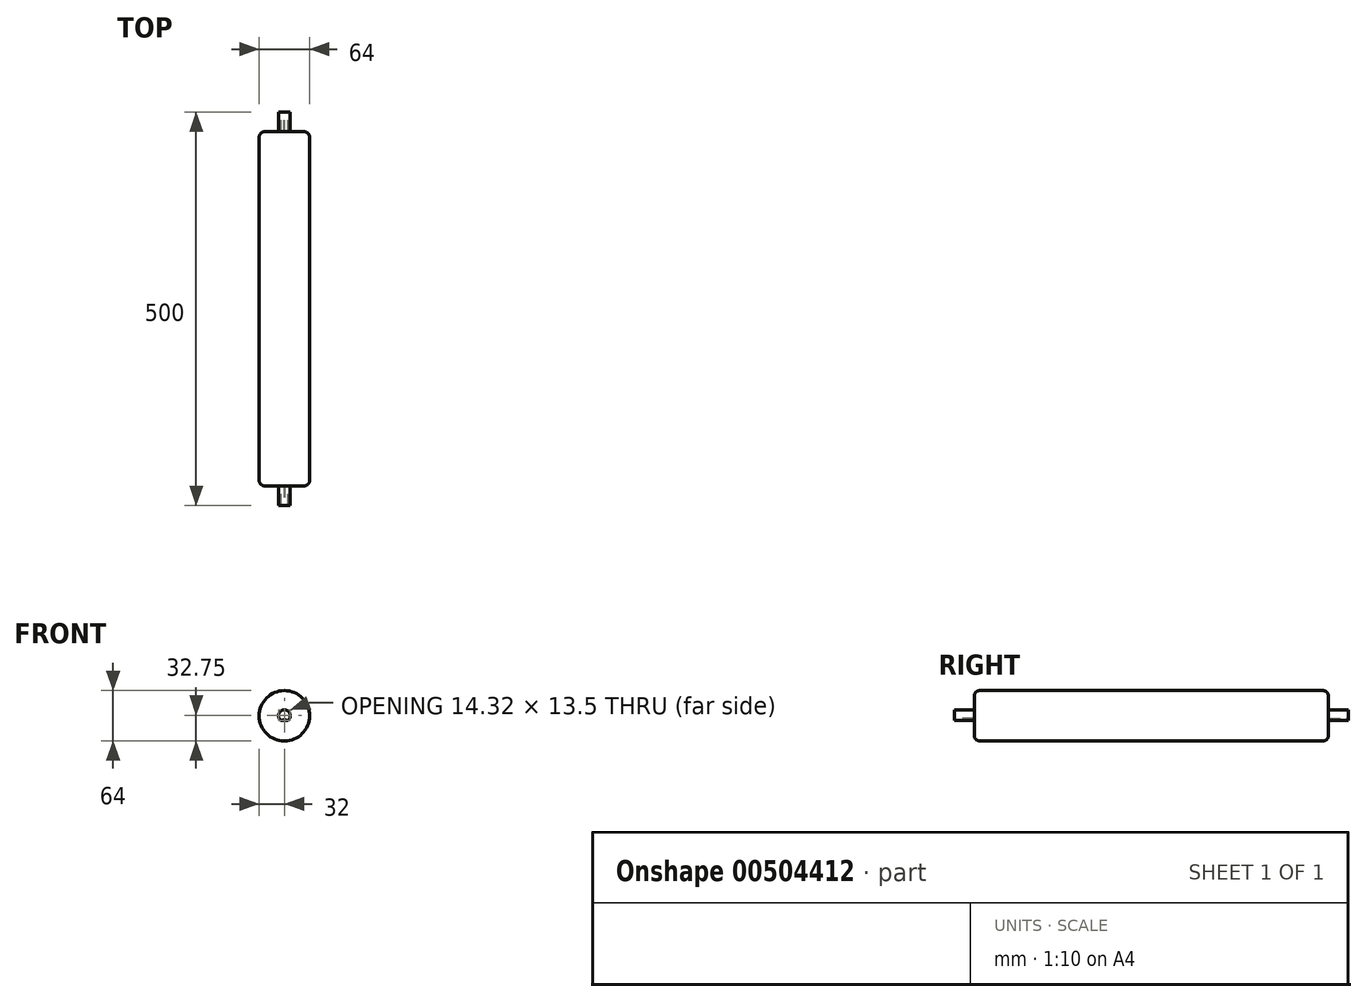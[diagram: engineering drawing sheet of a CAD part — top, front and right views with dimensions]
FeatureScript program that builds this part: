
annotation { "Feature Type Name" : "Feature", "Feature Type Description" : "" }
export const myFeature = defineFeature(function(context is Context, id is Id, definition is map)
    precondition{}
    {
        {
            var Q0;
            Q0=qCreatedBy(makeId("Right.planeOp"),FACE);
            var sketch = newSketch(context, id + "F0", { "sketchPlane" : qUnion([Q0])});
            skLineSegment(sketch, "E0", {"start": v(-237.76, 0) * mm, "end": v(-237.76, 7.5) * mm});
            skLineSegment(sketch, "E1", {"start": v(-237.76, 7.5) * mm, "end": v(-212.76, 7.5) * mm});
            skLineSegment(sketch, "E2", {"start": v(-212.76, 7.5) * mm, "end": v(-212.76, 32) * mm});
            skLineSegment(sketch, "E3", {"start": v(-212.76, 32) * mm, "end": v(237.24, 32) * mm});
            skLineSegment(sketch, "E4", {"start": v(237.24, 32) * mm, "end": v(237.24, 7.5) * mm});
            skLineSegment(sketch, "E5", {"start": v(237.24, 7.5) * mm, "end": v(262.24, 7.5) * mm});
            skLineSegment(sketch, "E6", {"start": v(262.24, 7.5) * mm, "end": v(262.24, 0) * mm});
            skLineSegment(sketch, "E7", {"start": v(262.24, 0) * mm, "end": v(-237.76, 0) * mm});
            skSolve(sketch);
        }
        {
            var Q0;
            Q0=makeQuery(id+"F0.imprint","IMPRINT",FACE,{"disambiguationData":[TD([[makeQuery(id+"F0.imprint","IMPRINT",EDGE,{"derivedFrom":sQuery(id+"F0.wireOp",EDGE,"E0")}),-1.0]])]});
            var Q1;
            Q1=sQuery(id+"F0.wireOp",EDGE,"E7");
            revolve(context, id + "F1", {"entities" : qUnion([Q0]), "axis" : qUnion([Q1]), "revolveType" : RevolveType.FULL});
        }
        {
            var Q0;
            Q0=makeQuery(id+"F1.opRevolve","SWEPT_EDGE",EDGE,{"disambiguationData":[OSD([sQuery(id+"F0.wireOp",EDGE,"E2"),sQuery(id+"F0.wireOp",EDGE,"E3")])]});
            var Q1;
            Q1=makeQuery(id+"F1.opRevolve","SWEPT_EDGE",EDGE,{"disambiguationData":[OSD([sQuery(id+"F0.wireOp",EDGE,"E3"),sQuery(id+"F0.wireOp",EDGE,"E4")])]});
            fillet(context, id + "F2", {"entities" : qUnion([Q0, Q1]), "radius" : 7 * mm, "tangentPropagation" : true, "allowEdgeOverflow" : false});
        }
        {
            var Q0;
            Q0=makeQuery(id+"F1.opRevolve","SWEPT_FACE",FACE,{"disambiguationData":[OSD([sQuery(id+"F0.wireOp",EDGE,"E0")])]});
            var sketch = newSketch(context, id + "F3", { "sketchPlane" : qUnion([Q0])});
            skLineSegment(sketch, "E8", {"start": v(-7.97, -6) * mm, "end": v(-0.5, -6) * mm});
            skLineSegment(sketch, "E9", {"start": v(-0.5, -6) * mm, "end": v(-0.5, -3.27) * mm});
            skLineSegment(sketch, "E10", {"start": v(-0.5, -3.27) * mm, "end": v(0.5, -3.27) * mm});
            skLineSegment(sketch, "E11", {"start": v(0.5, -3.27) * mm, "end": v(0.5, -6) * mm});
            skLineSegment(sketch, "E12", {"start": v(0.5, -6) * mm, "end": v(8.6, -6) * mm});
            skLineSegment(sketch, "E13", {"start": v(8.6, -6) * mm, "end": v(8.6, -10.85) * mm});
            skLineSegment(sketch, "E14", {"start": v(8.6, -10.85) * mm, "end": v(-7.77, -10.85) * mm});
            skLineSegment(sketch, "E15", {"start": v(-7.77, -10.85) * mm, "end": v(-7.97, -6) * mm});
            skSolve(sketch);
        }
        {
            var Q0;
            Q0 = qSketchRegion(id + "F3", true);
            var Q1;
            Q1=makeQuery(id+"F1.opRevolve","SWEPT_FACE",FACE,{"disambiguationData":[OSD([sQuery(id+"F0.wireOp",EDGE,"E2")])]});
            extrude(context, id + "F4", {"entities" : qUnion([Q0]), "operationType" : NewBodyOperationType.REMOVE, "endBound" : BoundingType.UP_TO_SURFACE, "oppositeDirection" : true, "depth" : 25 * mm, "endBoundEntityFace" : qUnion([Q1]), "offsetDistance" : 25 * mm});
        }
        {
            var Q0;
            Q0=makeQuery(id+"F1.opRevolve","SWEPT_FACE",FACE,{"disambiguationData":[OSD([sQuery(id+"F0.wireOp",EDGE,"E6")])]});
            var sketch = newSketch(context, id + "F5", { "sketchPlane" : qUnion([Q0])});
            skLineSegment(sketch, "E16", {"start": v(8.15, -6) * mm, "end": v(0.5, -6) * mm});
            skLineSegment(sketch, "E17", {"start": v(0.5, -6) * mm, "end": v(0.5, -3.27) * mm});
            skLineSegment(sketch, "E18", {"start": v(0.5, -3.27) * mm, "end": v(-0.5, -3.27) * mm});
            skLineSegment(sketch, "E19", {"start": v(-0.5, -3.27) * mm, "end": v(-0.5, -6) * mm});
            skLineSegment(sketch, "E20", {"start": v(-0.5, -6) * mm, "end": v(-9.72, -6) * mm});
            skLineSegment(sketch, "E21", {"start": v(-9.72, -6) * mm, "end": v(-10.43, -10.79) * mm});
            skLineSegment(sketch, "E22", {"start": v(-10.43, -10.79) * mm, "end": v(9.8, -10.29) * mm});
            skLineSegment(sketch, "E23", {"start": v(9.8, -10.29) * mm, "end": v(8.15, -6) * mm});
            skSolve(sketch);
        }
        {
            var Q0;
            Q0 = qSketchRegion(id + "F5", true);
            var Q1;
            Q1=makeQuery(id+"F1.opRevolve","SWEPT_FACE",FACE,{"disambiguationData":[OSD([sQuery(id+"F0.wireOp",EDGE,"E4")])]});
            extrude(context, id + "F6", {"entities" : qUnion([Q0]), "operationType" : NewBodyOperationType.REMOVE, "endBound" : BoundingType.UP_TO_SURFACE, "oppositeDirection" : true, "depth" : 25 * mm, "endBoundEntityFace" : qUnion([Q1]), "offsetDistance" : 25 * mm});
        }
    });
